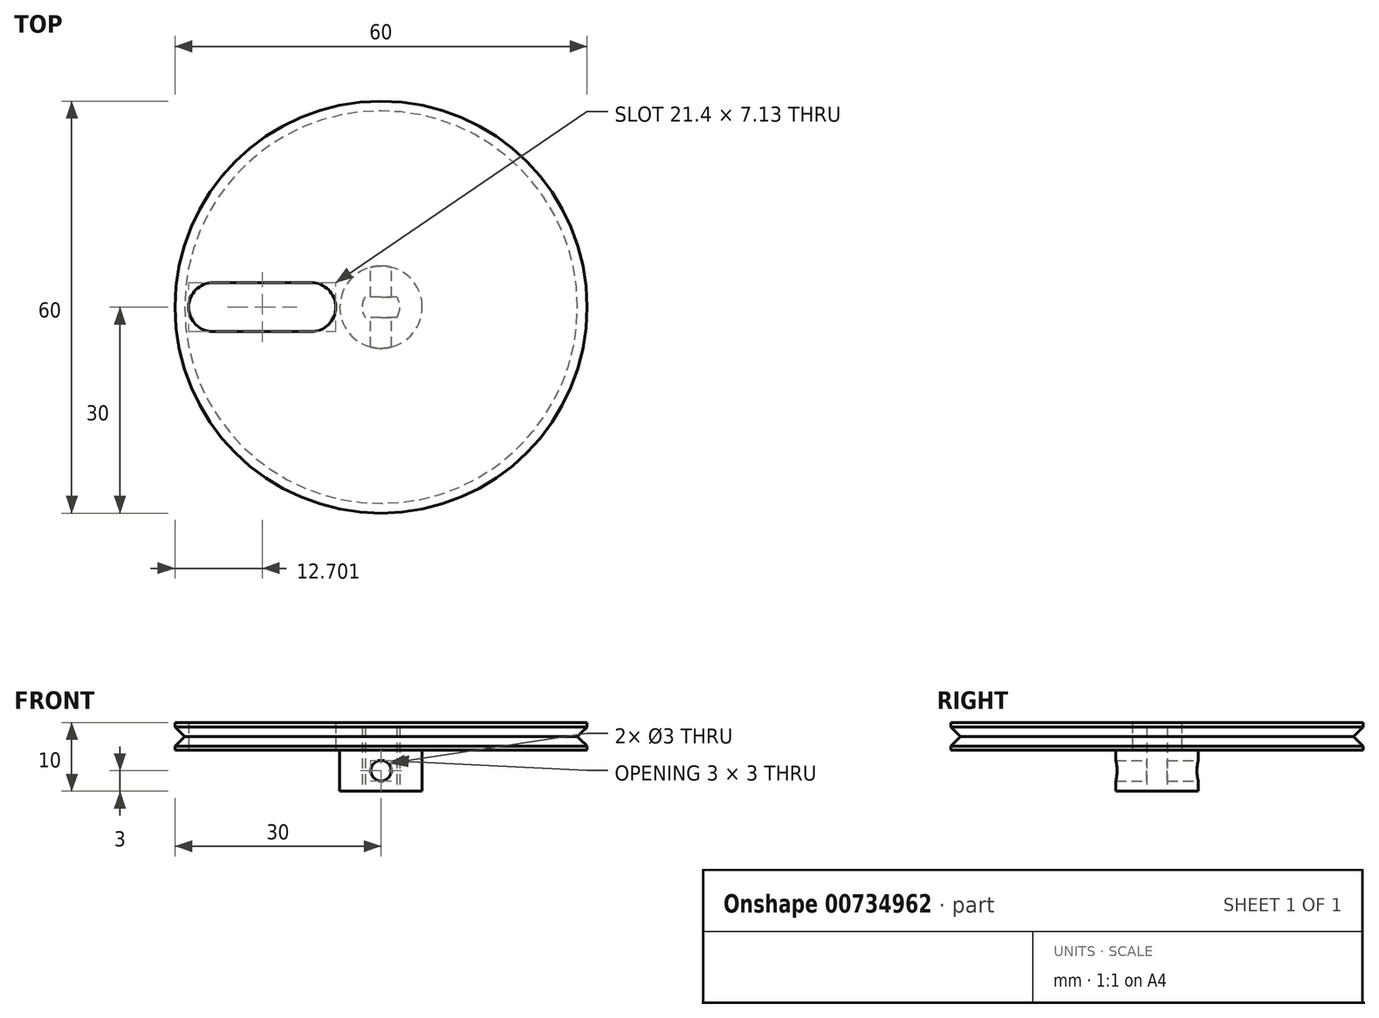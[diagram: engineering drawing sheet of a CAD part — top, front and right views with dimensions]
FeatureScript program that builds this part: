
annotation { "Feature Type Name" : "Feature", "Feature Type Description" : "" }
export const myFeature = defineFeature(function(context is Context, id is Id, definition is map)
    precondition{}
    {
        {
            var Q0;
            Q0=qCreatedBy(makeId("Top.planeOp"),FACE);
            var sketch = newSketch(context, id + "F0", { "sketchPlane" : qUnion([Q0])});
            skCircle(sketch, "E0", {"center": v(0, 0) * mm, "radius": 30 * mm});
            skCircle(sketch, "E1", {"center": v(0, 0) * mm, "radius": 6 * mm});
            skSolve(sketch);
        }
        {
            var Q0;
            Q0=qSketchRegion(id+"F0",true);
            var Q1;
            Q1=makeQuery(id+"F0.imprint","IMPRINT",FACE,{"disambiguationData":[TD([[makeQuery(id+"F0.imprint","IMPRINT",EDGE,{"derivedFrom":sQuery(id+"F0.wireOp",EDGE,"E1")}),1.0]])]});
            extrude(context, id + "F1", {"entities" : qUnion([Q0, Q1]), "depth" : 4 * mm, "offsetDistance" : 25 * mm});
        }
        {
            var Q0;
            Q0=makeQuery(id+"F0.imprint","IMPRINT",FACE,{"disambiguationData":[TD([[makeQuery(id+"F0.imprint","IMPRINT",EDGE,{"derivedFrom":sQuery(id+"F0.wireOp",EDGE,"E1")}),1.0]])]});
            extrude(context, id + "F2", {"entities" : qUnion([Q0]), "operationType" : NewBodyOperationType.ADD, "oppositeDirection" : true, "depth" : 6 * mm, "offsetDistance" : 25 * mm});
        }
        {
            var Q0;
            Q0=qCreatedBy(makeId("Front.planeOp"),FACE);
            var sketch = newSketch(context, id + "F3", { "sketchPlane" : qUnion([Q0])});
            skCircle(sketch, "E2", {"center": v(0, -3) * mm, "radius": 1.5 * mm});
            skSolve(sketch);
        }
        {
            var Q0;
            Q0=qSketchRegion(id+"F3",true);
            extrude(context, id + "F4", {"entities" : qUnion([Q0]), "operationType" : NewBodyOperationType.REMOVE, "endBound" : BoundingType.SYMMETRIC, "depth" : 26 * mm, "offsetDistance" : 25 * mm});
        }
        {
            var Q0;
            Q0=makeQuery(id+"F2.opExtrude","CAP_FACE",FACE,{"disambiguationData":[OSD([sQuery(id+"F0.wireOp",EDGE,"E1")])],"isStart":false});
            var sketch = newSketch(context, id + "F5", { "sketchPlane" : qUnion([Q0])});
            skLineSegment(sketch, "E3.bottom", {"start": v(2.3, 1.5) * mm, "end": v(-2.3, 1.5) * mm});
            skLineSegment(sketch, "E3.top", {"start": v(2.3, -1.5) * mm, "end": v(-2.3, -1.5) * mm});
            skLineSegment(sketch, "E3.left", {"start": v(2.3, 1.5) * mm, "end": v(2.3, -1.5) * mm});
            skLineSegment(sketch, "E3.right", {"start": v(-2.3, 1.5) * mm, "end": v(-2.3, -1.5) * mm});
            skPoint(sketch, "E3.middle", {"position": v(0, 0) * mm});
            skArc(sketch, "E4", {"start": v(2.3, -1.5) * mm, "mid": v(2.75, 0) * mm, "end": v(2.3, 1.5) * mm});
            skArc(sketch, "E5", {"start": v(-2.3, 1.5) * mm, "mid": v(-2.75, 0) * mm, "end": v(-2.3, -1.5) * mm});
            skSolve(sketch);
        }
        {
            var Q0;
            Q0=makeQuery(id+"F5.imprint","IMPRINT",FACE,{"disambiguationData":[TD([[makeQuery(id+"F5.imprint","IMPRINT",EDGE,{"derivedFrom":sQuery(id+"F5.wireOp",EDGE,"E3.left")}),1.0]])]});
            var Q1;
            Q1=makeQuery(id+"F5.imprint","IMPRINT",FACE,{"disambiguationData":[TD([[makeQuery(id+"F5.imprint","IMPRINT",EDGE,{"derivedFrom":sQuery(id+"F5.wireOp",EDGE,"E3.bottom")}),1.0]])]});
            var Q2;
            Q2=makeQuery(id+"F5.imprint","IMPRINT",FACE,{"disambiguationData":[TD([[makeQuery(id+"F5.imprint","IMPRINT",EDGE,{"derivedFrom":sQuery(id+"F5.wireOp",EDGE,"E3.right")}),-1.0]])]});
            extrude(context, id + "F6", {"entities" : qUnion([Q0, Q1, Q2]), "operationType" : NewBodyOperationType.REMOVE, "oppositeDirection" : true, "depth" : 9.4 * mm, "offsetDistance" : 25 * mm});
        }
        {
            var Q0;
            Q0=qCreatedBy(makeId("Front.planeOp"),FACE);
            var sketch = newSketch(context, id + "F7", { "sketchPlane" : qUnion([Q0])});
            skLineSegment(sketch, "E6", {"start": v(-30, -0.04) * mm, "end": v(-30, 4) * mm});
            skLineSegment(sketch, "E7", {"start": v(-30, 0) * mm, "end": v(-30, 3.96) * mm});
            skLineSegment(sketch, "E8", {"start": v(-30, 0.55) * mm, "end": v(-28.59, 1.96) * mm});
            skLineSegment(sketch, "E9", {"start": v(-28.59, 1.96) * mm, "end": v(-30, 3.38) * mm});
            skSolve(sketch);
        }
        {
            var Q0;
            Q0=qCreatedBy(makeId("Front.planeOp"),FACE);
            var sketch = newSketch(context, id + "F8", { "sketchPlane" : qUnion([Q0])});
            skLineSegment(sketch, "E10", {"start": v(0, -15.8) * mm, "end": v(0, 8.44) * mm, "construction": true});
            skSolve(sketch);
        }
        {
            var Q0;
            Q0=qSketchRegion(id+"F7",true);
            var Q1;
            Q1=qConstructionFilter(qBodyType(qCreatedBy(id+"F7",EDGE),BodyType.WIRE),ConstructionObject.NO);
            var Q2;
            Q2=sQuery(id+"F8.wireOp",EDGE,"E10");
            revolve(context, id + "F9", {"operationType" : NewBodyOperationType.REMOVE, "surfaceOperationType" : NewSurfaceOperationType.NEW, "entities" : qUnion([Q0]), "surfaceEntities" : qUnion([Q1]), "axis" : qUnion([Q2]), "revolveType" : RevolveType.FULL, "oppositeDirection" : true});
        }
        {
            var Q0;
            Q0=qCreatedBy(makeId("Top.planeOp"),FACE);
            var sketch = newSketch(context, id + "F10", { "sketchPlane" : qUnion([Q0])});
            skLineSegment(sketch, "E11.bottom", {"start": v(-24.43, -3.57) * mm, "end": v(-10.17, -3.57) * mm});
            skLineSegment(sketch, "E11.top", {"start": v(-24.43, 3.57) * mm, "end": v(-10.17, 3.57) * mm});
            skLineSegment(sketch, "E11.left", {"start": v(-24.43, -3.57) * mm, "end": v(-24.43, 3.57) * mm});
            skLineSegment(sketch, "E11.right", {"start": v(-10.17, -3.57) * mm, "end": v(-10.17, 3.57) * mm});
            skPoint(sketch, "E11.middle", {"position": v(-17.3, 0) * mm});
            skArc(sketch, "E12", {"start": v(-24.43, 3.57) * mm, "mid": v(-28, 0) * mm, "end": v(-24.43, -3.57) * mm});
            skArc(sketch, "E13", {"start": v(-10.17, -3.57) * mm, "mid": v(-6.6, 0) * mm, "end": v(-10.17, 3.57) * mm});
            skSolve(sketch);
        }
        {
            var Q0;
            Q0=qSketchRegion(id+"F10",true);
            extrude(context, id + "F11", {"entities" : qUnion([Q0]), "operationType" : NewBodyOperationType.REMOVE, "endBound" : BoundingType.SYMMETRIC, "depth" : 25 * mm, "offsetDistance" : 25 * mm});
        }
        {
            var Q0;
            Q0=qCreatedBy(makeId("Right.planeOp"),FACE);
            var sketch = newSketch(context, id + "F12", { "sketchPlane" : qUnion([Q0])});
            skLineSegment(sketch, "E14", {"start": v(0, 19.52) * mm, "end": v(0, -29.35) * mm});
            skSolve(sketch);
        }
    });
